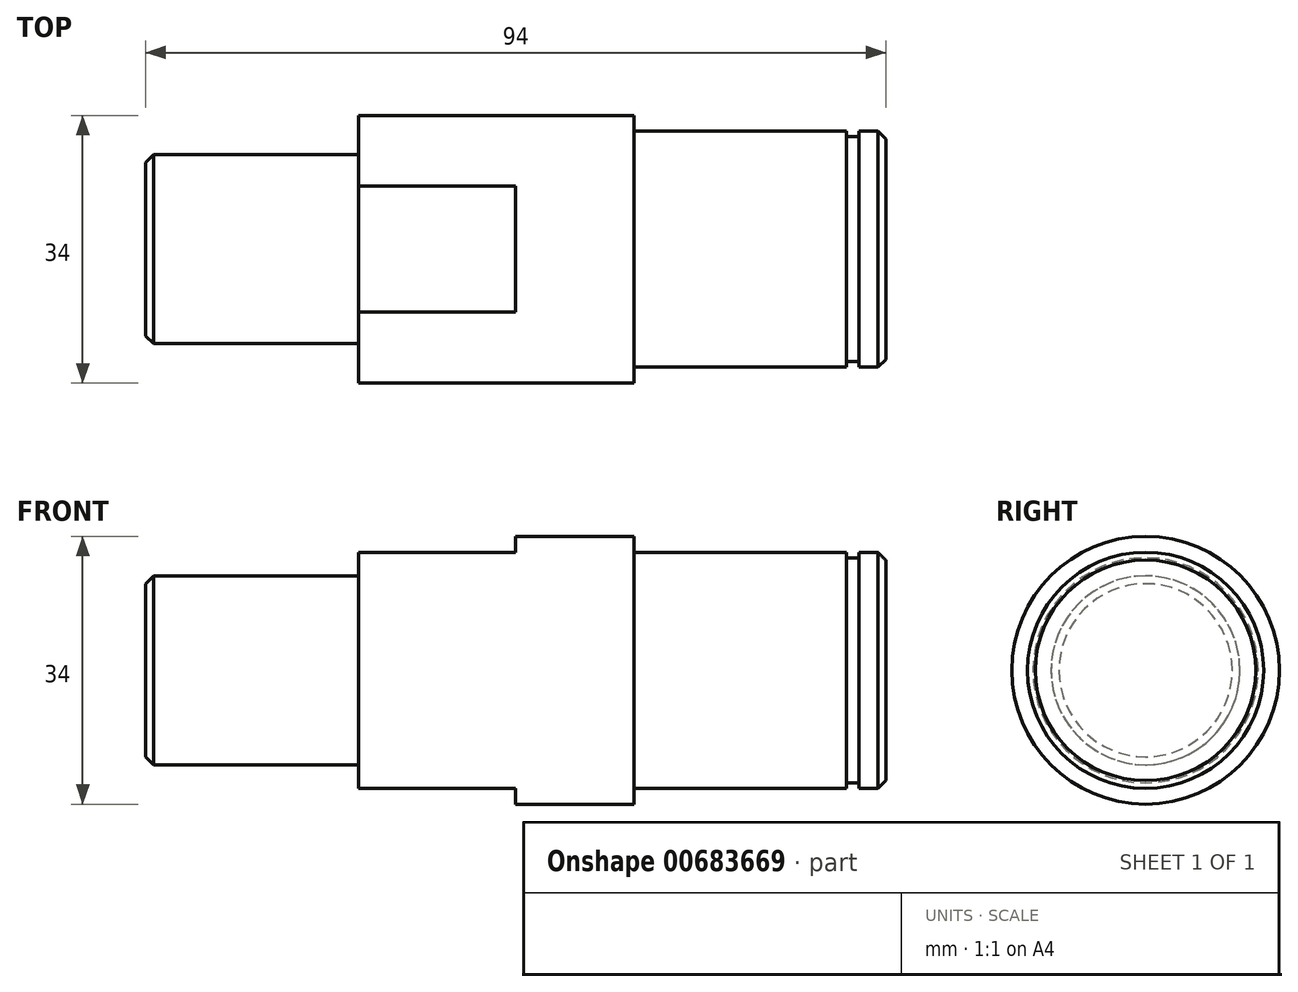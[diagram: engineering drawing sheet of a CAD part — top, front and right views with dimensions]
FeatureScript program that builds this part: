
annotation { "Feature Type Name" : "Feature", "Feature Type Description" : "" }
export const myFeature = defineFeature(function(context is Context, id is Id, definition is map)
    precondition{}
    {
        {
            var Q0;
            Q0=qCreatedBy(makeId("Front.planeOp"),FACE);
            var sketch = newSketch(context, id + "F0", { "sketchPlane" : qUnion([Q0])});
            skLineSegment(sketch, "E0", {"start": v(0, 0) * mm, "end": v(94, 0) * mm});
            skLineSegment(sketch, "E1", {"start": v(94, 0) * mm, "end": v(94, 15) * mm});
            skLineSegment(sketch, "E2", {"start": v(94, 15) * mm, "end": v(90.6, 15) * mm});
            skLineSegment(sketch, "E3", {"start": v(90.6, 15) * mm, "end": v(90.6, 14.3) * mm});
            skLineSegment(sketch, "E4", {"start": v(90.6, 14.3) * mm, "end": v(89, 14.3) * mm});
            skLineSegment(sketch, "E5", {"start": v(89, 14.3) * mm, "end": v(89, 15) * mm});
            skLineSegment(sketch, "E6", {"start": v(89, 15) * mm, "end": v(62, 15) * mm});
            skLineSegment(sketch, "E7", {"start": v(62, 15) * mm, "end": v(62, 17) * mm});
            skLineSegment(sketch, "E8", {"start": v(62, 17) * mm, "end": v(27, 17) * mm});
            skLineSegment(sketch, "E9", {"start": v(27, 12) * mm, "end": v(0, 12) * mm});
            skLineSegment(sketch, "E10", {"start": v(0, 12) * mm, "end": v(0, 0) * mm});
            skLineSegment(sketch, "E11", {"start": v(27, 17) * mm, "end": v(27, 12) * mm});
            skSolve(sketch);
        }
        {
            var Q0;
            Q0=makeQuery(id+"F0.imprint","IMPRINT",FACE,{"disambiguationData":[TD([[makeQuery(id+"F0.imprint","IMPRINT",EDGE,{"derivedFrom":sQuery(id+"F0.wireOp",EDGE,"E0")}),1.0]])]});
            var Q1;
            Q1=sQuery(id+"F0.wireOp",EDGE,"E0");
            revolve(context, id + "F1", {"entities" : qUnion([Q0]), "axis" : qUnion([Q1]), "revolveType" : RevolveType.FULL});
        }
        {
            var Q0;
            Q0=makeQuery(id+"F1.opRevolve","SWEPT_EDGE",EDGE,{"disambiguationData":[OSD([sQuery(id+"F0.wireOp",EDGE,"E1"),sQuery(id+"F0.wireOp",EDGE,"E2")])]});
            chamfer(context, id + "F2", {"entities" : qUnion([Q0]), "width" : 1 * mm, "tangentPropagation" : true});
        }
        {
            var Q0;
            Q0=makeQuery(id+"F1.opRevolve","SWEPT_EDGE",EDGE,{"disambiguationData":[OSD([sQuery(id+"F0.wireOp",EDGE,"E9"),sQuery(id+"F0.wireOp",EDGE,"E10")])]});
            chamfer(context, id + "F3", {"entities" : qUnion([Q0]), "width" : 1 * mm, "tangentPropagation" : true});
        }
        {
            var Q0;
            Q0=qCreatedBy(makeId("Front.planeOp"),FACE);
            var sketch = newSketch(context, id + "F4", { "sketchPlane" : qUnion([Q0])});
            skLineSegment(sketch, "E12", {"start": v(25.41, 15) * mm, "end": v(47, 15) * mm});
            skLineSegment(sketch, "E13.0", {"start": v(27, -17) * mm, "end": v(27, 17) * mm});
            skLineSegment(sketch, "E14.0", {"start": v(47, -17) * mm, "end": v(47, 15) * mm});
            skLineSegment(sketch, "E15", {"start": v(47, 15) * mm, "end": v(47, 20.84) * mm});
            skLineSegment(sketch, "E16", {"start": v(47, 20.84) * mm, "end": v(25.73, 20.84) * mm});
            skLineSegment(sketch, "E17", {"start": v(25.73, 20.84) * mm, "end": v(25.41, 15) * mm});
            skLineSegment(sketch, "E18.MirrorCS", {"start": v(47, -20.84) * mm, "end": v(25.73, -20.84) * mm});
            skLineSegment(sketch, "E19.MirrorCS", {"start": v(25.73, -20.84) * mm, "end": v(25.41, -15) * mm});
            skLineSegment(sketch, "E20.MirrorCS", {"start": v(25.41, -15) * mm, "end": v(47, -15) * mm});
            skLineSegment(sketch, "E21.MirrorCS", {"start": v(47, -15) * mm, "end": v(47, -20.84) * mm});
            skSolve(sketch);
        }
        {
            var Q0;
            {var subQ0=sQuery(id+"F4.wireOp",EDGE,"E15");Q0=makeQuery(id+"F4.imprint","IMPRINT",FACE,{"disambiguationData":[TD([[makeQuery(id+"F4.imprint","IMPRINT",EDGE,{"derivedFrom":subQ0}),1.0]])]});}
            var Q1;
            {var subQ5=sQuery(id+"F4.wireOp",EDGE,"E18.MirrorCS");Q1=makeQuery(id+"F4.imprint","IMPRINT",FACE,{"disambiguationData":[TD([[makeQuery(id+"F4.imprint","IMPRINT",EDGE,{"derivedFrom":subQ5}),-1.0]])]});}
            extrude(context, id + "F5", {"entities" : qUnion([Q0, Q1]), "operationType" : NewBodyOperationType.REMOVE, "oppositeDirection" : true, "depth" : 25 * mm, "offsetDistance" : 25 * mm, "symmetric" : true});
        }
    });
